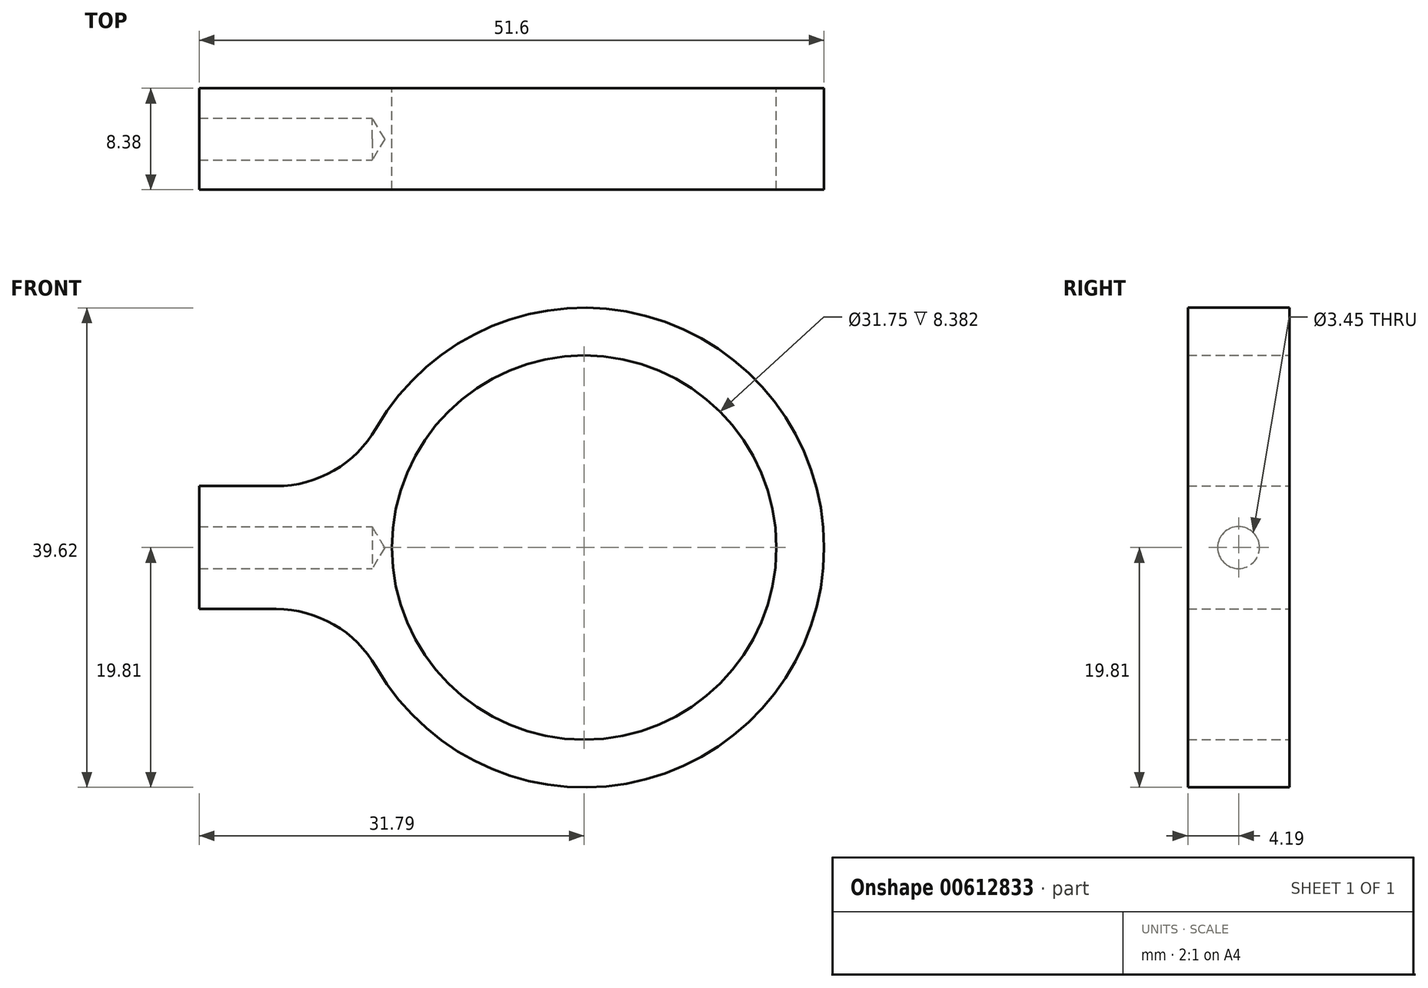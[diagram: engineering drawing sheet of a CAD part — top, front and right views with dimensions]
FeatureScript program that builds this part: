
annotation { "Feature Type Name" : "Feature", "Feature Type Description" : "" }
export const myFeature = defineFeature(function(context is Context, id is Id, definition is map)
    precondition{}
    {
        {
            var Q0;
            Q0=qCreatedBy(makeId("Front.planeOp"),FACE);
            var sketch = newSketch(context, id + "F0", { "sketchPlane" : qUnion([Q0])});
            skCircle(sketch, "E0", {"center": v(0, 0) * mm, "radius": 15.88 * mm});
            skArc(sketch, "E1", {"start": v(-17.18, 9.86) * mm, "mid": v(19.81, 0) * mm, "end": v(-17.18, -9.86) * mm});
            skLineSegment(sketch, "E2", {"start": v(-25.44, -5.08) * mm, "end": v(-31.8, -5.08) * mm});
            skLineSegment(sketch, "E3", {"start": v(-31.8, -5.08) * mm, "end": v(-31.8, 5.08) * mm});
            skLineSegment(sketch, "E4", {"start": v(-31.8, 5.08) * mm, "end": v(-25.44, 5.08) * mm});
            skPoint(sketch, "E5", {"position": v(-31.8, 0) * mm});
            skPoint(sketch, "E6.visualSharp", {"position": v(-19.15, 5.08) * mm});
            skArc(sketch, "E6.filletArc", {"start": v(-25.44, 5.08) * mm, "mid": v(-20.67, 6.36) * mm, "end": v(-17.18, 9.86) * mm});
            skPoint(sketch, "E7.visualSharp", {"position": v(-19.15, -5.08) * mm});
            skArc(sketch, "E7.filletArc", {"start": v(-17.18, -9.86) * mm, "mid": v(-20.67, -6.36) * mm, "end": v(-25.44, -5.08) * mm});
            skSolve(sketch);
        }
        {
            var Q0;
            Q0=qSketchRegion(id+"F0",true);
            extrude(context, id + "F1", {"entities" : qUnion([Q0]), "depth" : 8.38 * mm, "symmetric" : true});
        }
        {
            var Q0;
            Q0=makeQuery(id+"F1.opExtrude","SWEPT_FACE",FACE,{"disambiguationData":[OSD([sQuery(id+"F0.wireOp",EDGE,"E3")])]});
            var sketch = newSketch(context, id + "F2", { "sketchPlane" : qUnion([Q0])});
            skPoint(sketch, "E8", {"position": v(0, 0) * mm});
            skSolve(sketch);
        }
        {
            var Q0;
            Q0=sQuery(id+"F2.wireOp",VERTEX,"E8");
            var Q1;
            Q1=makeQuery(id+"F1.opExtrude","SWEPT_BODY",BODY,{"disambiguationData":[OSD([sQuery(id+"F0.wireOp",EDGE,"E0"),sQuery(id+"F0.wireOp",EDGE,"E1"),sQuery(id+"F0.wireOp",EDGE,"E2"),sQuery(id+"F0.wireOp",EDGE,"E3"),sQuery(id+"F0.wireOp",EDGE,"E4"),sQuery(id+"F0.wireOp",EDGE,"E6.filletArc"),sQuery(id+"F0.wireOp",EDGE,"E7.filletArc")])]});
            hole(context, id + "F3", {"style" : HoleStyle.SIMPLE, "holeDiameter" : 3.45 * mm, "endStyle" : HoleEndStyle.BLIND, "holeDepth" : 14.29 * mm, "locations" : qUnion([Q0]), "scope" : qUnion([Q1])});
        }
    });
